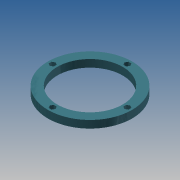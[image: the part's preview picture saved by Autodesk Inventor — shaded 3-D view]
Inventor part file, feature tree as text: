
AUTODESK INVENTOR PART (.ipt)
format: ipt  version: 2013 (Build 170138000, 138)  size: 123,392 bytes
history: native  units: mm
features: extrude x3, sketch x3, pattern_circular x1
ambient origin geometry x8: Origin, YZ Plane, XZ Plane, XY Plane, X Axis, Y Axis, Z Axis, Center Point
bodies: Solid1 (feature_tree)
feature tree (7):
  extrude  "Extrusion1"  Depth=90.0mm
  extrude  "Extrusion2"  Depth=40.0mm
  extrude  "Extrusion3"  Depth=10.0mm TaperAngle=0.0deg
  pattern_circular  "Circular Pattern1"  [2 undecoded]
  sketch  "Sketch1"  dims[d0=70.0mm d2=90.0mm]
  sketch  "Sketch2"  dims[d3=8.0mm d4=0.0mm d5=40.0mm]
  sketch  "Sketch3"  dims[d6=3.5mm d7=10.0mm d8=0.0mm d9=5.5mm d10=4.0mm d11=0.0mm d12=40.0mm d13=360.0deg]
note: 2 required parameter values undecoded (feature->parameter linkage not recoverable at this tier; creation-order binding heuristic only, values carry confidence <= 0.55)
